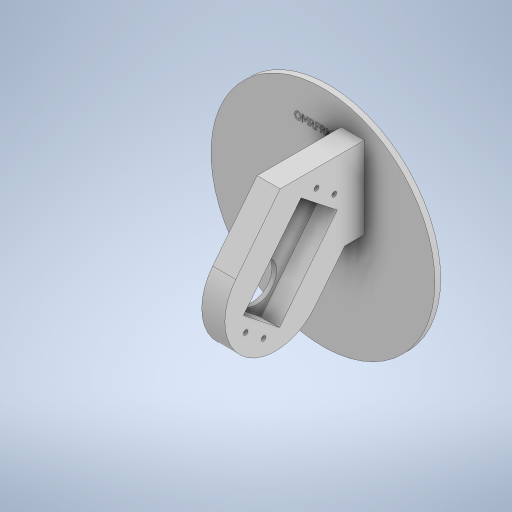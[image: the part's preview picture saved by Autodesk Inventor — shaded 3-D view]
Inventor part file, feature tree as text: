
AUTODESK INVENTOR PART (.ipt)
format: ipt  version: 2023.2 (Build 272271000, 271)  size: 459,264 bytes
history: native  units: mm
features: sketch x7, extrude x3, hole x3, emboss x1, plane x1
ambient origin geometry x8: Origin, YZ Plane, XZ Plane, XY Plane, X Axis, Y Axis, Z Axis, Center Point
bodies: Solid1 (feature_tree)
feature tree (15):
  extrude  "Extrusion1"  Depth=2.5mm TaperAngle=0.0deg
  hole  "Hole1"  [1 undecoded]
  hole  "Hole2"  [1 undecoded]
  emboss  "Emboss1"
  plane  "Work Plane1"
  extrude  "Extrusion2"  Depth=40.3mm
  extrude  "Extrusion3"  Depth=7.0mm
  hole  "Hole3"  [1 undecoded]
  sketch  "Sketch1"  dims[d0=97.0mm d1=2.5mm d2=0.0mm]
  sketch  "Sketch2"  dims[d3=15.0mm]
  sketch  "Sketch3"  dims[d4=2.1mm d5=6.0mm d6=4.0mm d7=2.0mm d8=90.0deg d9=8.0mm d10=0.0mm]
  sketch  "Sketch4"  dims[d11=8.0mm d12=6.0mm d13=4.0mm d14=2.0mm d15=90.0deg d16=8.0mm d17=0.0mm d18=1.0mm d19=0.0mm]
  sketch  "Sketch5"  dims[d20=8.0mm d21=19.9mm]
  sketch  "Sketch6"  dims[d22=40.3mm d23=9.85mm]
  sketch  "Sketch7"  dims[d24=17.0mm d25=54.0mm d26=2.5mm d27=2.5mm d28=10.0mm d29=0.0mm d30=19.9mm d31=40.3mm d32=9.85mm d33=17.0mm d34=54.0mm d35=2.5mm d36=2.5mm d37=8.0mm d38=0.0mm d39=49.422mm d40=9.85mm d41=2.0mm d42=6.0mm d43=4.0mm d44=2.0mm d45=90.0deg d46=7.0mm d47=0.0mm d48=15.419mm d49=35.158mm d50=35.158mm d51=9.85mm d52=15.419mm d54=9.85mm]
note: 3 required parameter values undecoded (feature->parameter linkage not recoverable at this tier; creation-order binding heuristic only, values carry confidence <= 0.55)
